# Revit family: Toilet-Floor_Mount-KOHLER-Numi-K-3901
name_source: partatom
category: Plumbing Fixtures
revit_build: Autodesk Revit 2015 (Build: 20140606_1530(x64)
units: mm (PartAtom-declared; Revit-internal decimal feet)

## types (3) — shared parameters
ADA Compliant = No
Apparent Load = 1800 VA
Assembly Code = D2010100
CW Connection = Yes
Cold Water Inlet = Cold Water Inlet
Date Modified = 12/11/2018
Default Elevation = 0"
Electrical Connector = Yes
Electrical Note = One dedicated circuit required, protected with Class A Ground-Fault Circuit-Interrupter (GFCI) or Residual Current Device (RCD)
Flow Rate = 0 GPM
Flush Rate = 1.28 gpf
HW Connection = No
Height = 17 7/8"
Hot Water Inlet = Hot Water Inlet
Length = 25 3/4"
Manufacturer = KOHLER Co.
MasterFormat 1995 = 15410
MasterFormat 2004 = 22.41.13
Material = Vitreous China
Pressure = 80.00 psi
Product Documentation Link = http://www.us.kohler.com
Product Name = Numi
Product Page URL = http://www.us.kohler.com
Rough-In = 12"
Seat Included = No
URL = https://www.us.kohler.com
Vent Connection = No
Voltage = 120 V
Waste Connection = Yes
Waste Water Outlet = Waste Water Outlet
Width = 14 1/2"

## per-type parameters (varying)
| type | Description | Finish | Model | Premium remote | Standard remote | Type |
| Premium remote, 0-White | Comfort Height one-piece elongated dual-flush intelligent toilet with skirted trapway and premium remote | Kohler-Vitreous_China-0-White | K-3901-NPR-0 | Yes | No | 1 |
| Premium remote, HB1-Honed Black | Comfort Height one-piece elongated dual-flush intelligent toilet with skirted trapway and premium remote | Kohler-Vitreous_China-HB1-Honed_Black | K-3901-NPR-HB1 | Yes | No | 2 |
| Standard remote, 0-White | Comfort Height one-piece elongated dual-flush intelligent toilet with skirted trapway and standard remote | Kohler-Vitreous_China-0-White | K-3901-NSR-0 | No | Yes | 3 |

## geometry (parser evidence)
native form markers: Sweep x9
no freeform markers — native parametric forms only
